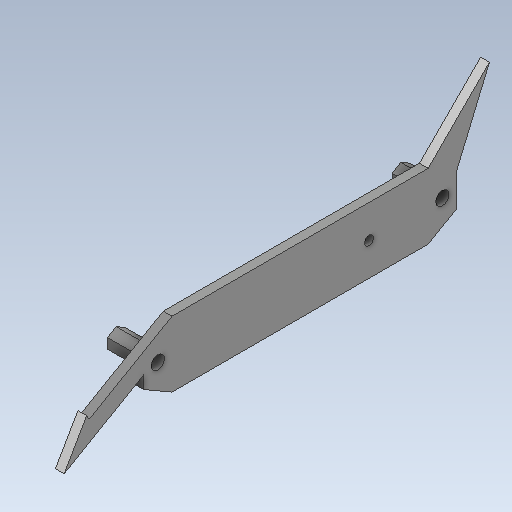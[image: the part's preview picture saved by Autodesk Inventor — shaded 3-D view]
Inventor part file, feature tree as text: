
AUTODESK INVENTOR PART (.ipt)
format: ipt  version: 2020 (Build 240168000, 168)  size: 156,672 bytes
history: native  units: in
note: dims shown in document units (in); Inventor stores cm internally (conversion verified against a paired STEP export)
features: other x3, extrude x2, sketch x2
ambient origin geometry x8: Origin, YZ Plane, XZ Plane, XY Plane, X Axis, Y Axis, Z Axis, Center Point
bodies: Solid1 (feature_tree)
feature tree (7):
  other  "HexWheelGuard.ipt"
  extrude  "Extrusion1"  Depth=0.315in
  extrude  "Extrusion2"  Depth=0.3937in
  other  "Solid1::HexWheelGuard.ipt"
  other  "TaggingFeature2"
  sketch  "Sketch1"  dims[d1=0.3937in d2=0.315in]
  sketch  "Sketch2"  dims[d3=60.0deg d4=1.4843in d5=0.0787in d6=0.3937in d7=0.0in d10=0.5906in d11=1.1024in d12=0.3937in d13=0.0in]
